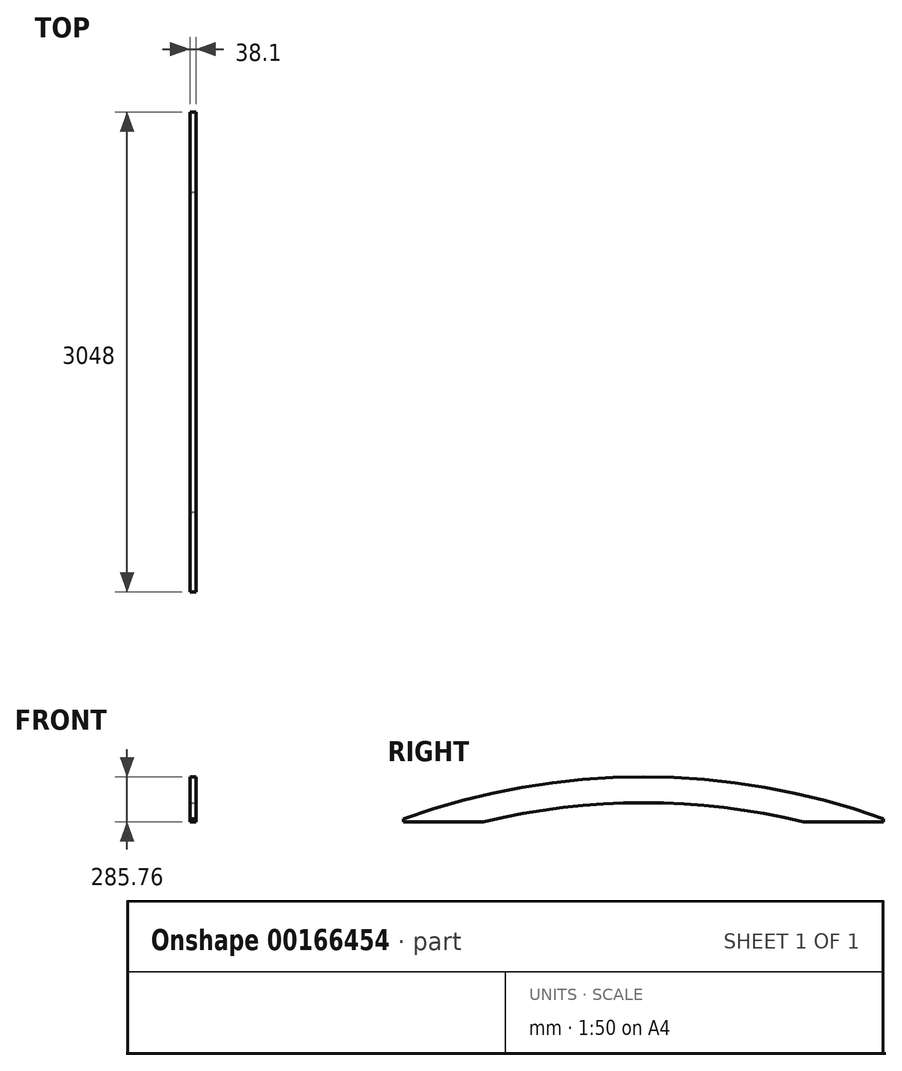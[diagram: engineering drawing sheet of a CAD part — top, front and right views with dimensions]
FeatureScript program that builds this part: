
annotation { "Feature Type Name" : "Feature", "Feature Type Description" : "" }
export const myFeature = defineFeature(function(context is Context, id is Id, definition is map)
    precondition{}
    {
        {
            var Q0;
            Q0=qCreatedBy(makeId("Front.planeOp"),FACE);
            var sketch = newSketch(context, id + "F0", { "sketchPlane" : qUnion([Q0])});
            skLineSegment(sketch, "E0.bottom", {"start": v(-19.05, 142.87) * mm, "end": v(19.05, 142.87) * mm});
            skLineSegment(sketch, "E0.top", {"start": v(-19.05, -142.88) * mm, "end": v(19.05, -142.88) * mm});
            skLineSegment(sketch, "E0.left", {"start": v(-19.05, 142.87) * mm, "end": v(-19.05, -142.88) * mm});
            skLineSegment(sketch, "E0.right", {"start": v(19.05, 142.87) * mm, "end": v(19.05, -142.88) * mm});
            skLineSegment(sketch, "E1", {"start": v(19.05, 142.88) * mm, "end": v(-19.05, -142.88) * mm, "construction": true});
            skSolve(sketch);
        }
        {
            var Q0;
            Q0 = qSketchRegion(id + "F0", true);
            extrude(context, id + "F1", {"entities" : qUnion([Q0]), "endBound" : BoundingType.SYMMETRIC, "depth" : 3048 * mm});
        }
        {
            var Q0;
            Q0=makeQuery(id+"F1.opExtrude","SWEPT_FACE",FACE,{"disambiguationData":[OSD([sQuery(id+"F0.wireOp",EDGE,"E0.left")])]});
            var sketch = newSketch(context, id + "F2", { "sketchPlane" : qUnion([Q0])});
            skArc(sketch, "E2", {"start": v(0, 142.88) * mm, "mid": v(-773.58, 75.7) * mm, "end": v(-1524, -123.82) * mm});
            skLineSegment(sketch, "E3", {"start": v(0, 476.36) * mm, "end": v(0, -370.91) * mm, "construction": true});
            skArc(sketch, "E4.MirrorCS", {"start": v(0, 142.88) * mm, "mid": v(773.58, 75.7) * mm, "end": v(1524, -123.82) * mm});
            skLineSegment(sketch, "E5", {"start": v(-1524, -123.83) * mm, "end": v(-1570.6, -123.83) * mm});
            skLineSegment(sketch, "E6", {"start": v(-1570.6, -123.83) * mm, "end": v(-1570.6, 303.4) * mm});
            skLineSegment(sketch, "E7", {"start": v(-1570.6, 303.4) * mm, "end": v(1568.75, 303.4) * mm});
            skLineSegment(sketch, "E8", {"start": v(1568.75, 303.4) * mm, "end": v(1568.75, -123.83) * mm});
            skLineSegment(sketch, "E9", {"start": v(1568.75, -123.83) * mm, "end": v(1524, -123.83) * mm});
            skSolve(sketch);
        }
        {
            var Q0;
            Q0 = qSketchRegion(id + "F2", true);
            extrude(context, id + "F3", {"entities" : qUnion([Q0]), "operationType" : NewBodyOperationType.REMOVE, "endBound" : BoundingType.THROUGH_ALL, "oppositeDirection" : true, "depth" : 25.4 * mm});
        }
        {
            var Q0;
            Q0=makeQuery(id+"F1.opExtrude","SWEPT_FACE",FACE,{"disambiguationData":[OSD([sQuery(id+"F0.wireOp",EDGE,"E0.right")])]});
            var sketch = newSketch(context, id + "F4", { "sketchPlane" : qUnion([Q0])});
            skArc(sketch, "E10", {"start": v(1016, -142.88) * mm, "mid": v(0, -21.79) * mm, "end": v(-1016, -142.88) * mm});
            skLineSegment(sketch, "E11", {"start": v(-1016, -142.88) * mm, "end": v(-1016, -481.72) * mm});
            skLineSegment(sketch, "E12", {"start": v(-1016, -481.72) * mm, "end": v(1016.47, -481.72) * mm});
            skLineSegment(sketch, "E13", {"start": v(1016.47, -481.72) * mm, "end": v(1016, -142.88) * mm});
            skSolve(sketch);
        }
        {
            var Q0;
            Q0 = qSketchRegion(id + "F4", true);
            extrude(context, id + "F5", {"entities" : qUnion([Q0]), "operationType" : NewBodyOperationType.REMOVE, "endBound" : BoundingType.THROUGH_ALL, "oppositeDirection" : true, "depth" : 25.4 * mm});
        }
    });
